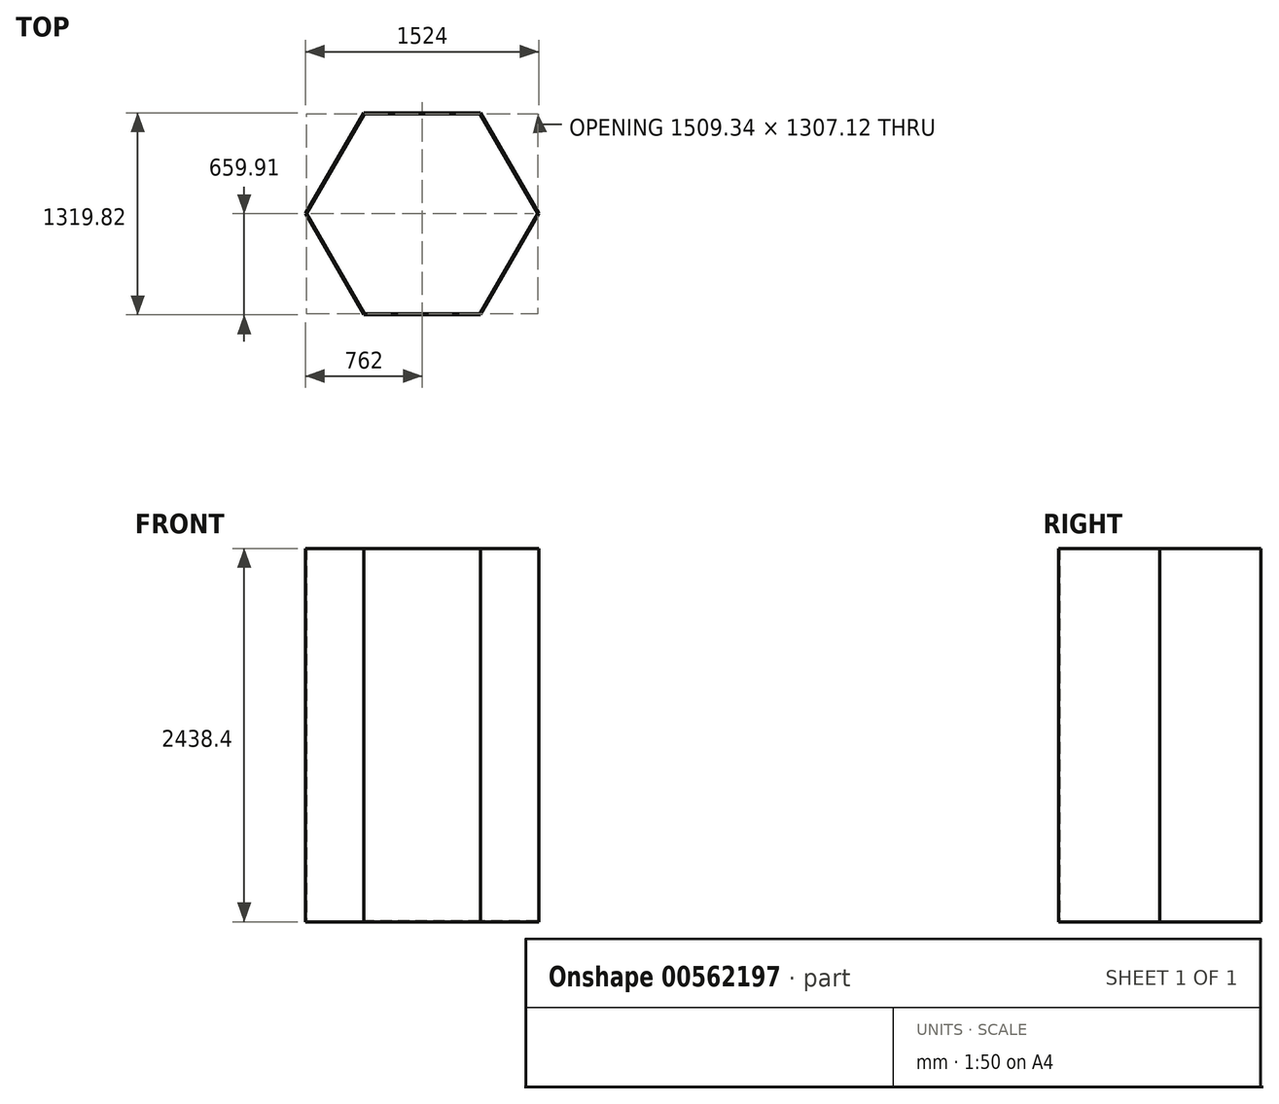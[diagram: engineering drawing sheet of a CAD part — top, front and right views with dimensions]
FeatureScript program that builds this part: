
annotation { "Feature Type Name" : "Feature", "Feature Type Description" : "" }
export const myFeature = defineFeature(function(context is Context, id is Id, definition is map)
    precondition{}
    {
        {
            var Q0;
            Q0=qCreatedBy(makeId("Top.planeOp"),FACE);
            var sketch = newSketch(context, id + "F0", { "sketchPlane" : qUnion([Q0])});
            skCircle(sketch, "E0.cCircle", {"center": v(0, 0) * mm, "radius": 762 * mm, "construction": true});
            skLineSegment(sketch, "E0.0", {"start": v(-762, 0) * mm, "end": v(-381, 659.91) * mm});
            skLineSegment(sketch, "E0.1", {"start": v(-381, 659.91) * mm, "end": v(381, 659.91) * mm});
            skLineSegment(sketch, "E0.2", {"start": v(381, 659.91) * mm, "end": v(762, 0) * mm});
            skLineSegment(sketch, "E0.3", {"start": v(762, 0) * mm, "end": v(381, -659.91) * mm});
            skLineSegment(sketch, "E0.4", {"start": v(381, -659.91) * mm, "end": v(-381, -659.91) * mm});
            skLineSegment(sketch, "E0.5", {"start": v(-381, -659.91) * mm, "end": v(-762, 0) * mm});
            skSolve(sketch);
        }
        {
            var Q0;
            Q0=makeQuery(id+"F0.imprint","IMPRINT",FACE,{"disambiguationData":[TD([[makeQuery(id+"F0.imprint","IMPRINT",EDGE,{"derivedFrom":sQuery(id+"F0.wireOp",EDGE,"E0.0")}),-1.0]])]});
            extrude(context, id + "F1", {"entities" : qUnion([Q0]), "depth" : 2438.4 * mm, "offsetDistance" : 25.4 * mm});
        }
        {
            var Q0;
            Q0=makeQuery(id+"F1.opExtrude","CAP_FACE",FACE,{"disambiguationData":[OSD([sQuery(id+"F0.wireOp",EDGE,"E0.0"),sQuery(id+"F0.wireOp",EDGE,"E0.1"),sQuery(id+"F0.wireOp",EDGE,"E0.2"),sQuery(id+"F0.wireOp",EDGE,"E0.3"),sQuery(id+"F0.wireOp",EDGE,"E0.4"),sQuery(id+"F0.wireOp",EDGE,"E0.5")])],"isStart":false});
            shell(context, id + "F2", {"entities" : qUnion([Q0]), "thickness" : 6.35 * mm});
        }
    });
